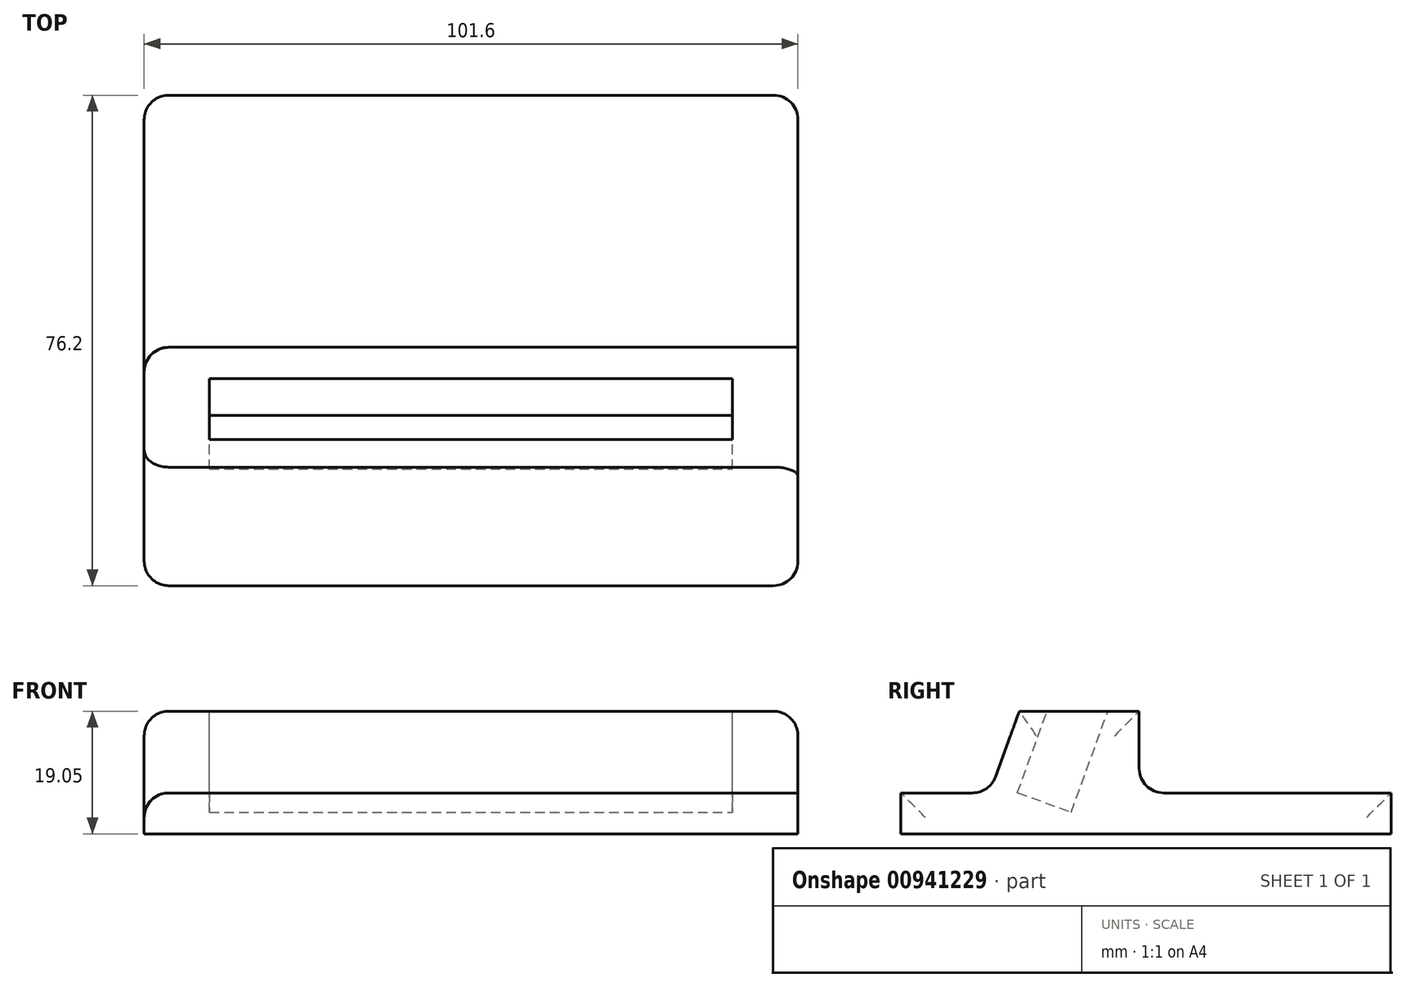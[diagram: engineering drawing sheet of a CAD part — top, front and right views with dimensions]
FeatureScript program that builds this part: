
annotation { "Feature Type Name" : "Feature", "Feature Type Description" : "" }
export const myFeature = defineFeature(function(context is Context, id is Id, definition is map)
    precondition{}
    {
        {
            var Q0;
            Q0=qCreatedBy(makeId("Top.planeOp"),FACE);
            var sketch = newSketch(context, id + "F0", { "sketchPlane" : qUnion([Q0])});
            skLineSegment(sketch, "E0.bottom", {"start": v(-54.82, -43.76) * mm, "end": v(46.78, -43.76) * mm});
            skLineSegment(sketch, "E0.top", {"start": v(-54.82, 32.44) * mm, "end": v(46.78, 32.44) * mm});
            skLineSegment(sketch, "E0.left", {"start": v(-54.82, -43.76) * mm, "end": v(-54.82, 32.44) * mm});
            skLineSegment(sketch, "E0.right", {"start": v(46.78, -43.76) * mm, "end": v(46.78, 32.44) * mm});
            skSolve(sketch);
        }
        {
            var Q0;
            Q0=makeQuery(id+"F0.imprint","IMPRINT",FACE,{"disambiguationData":[TD([[makeQuery(id+"F0.imprint","IMPRINT",EDGE,{"derivedFrom":sQuery(id+"F0.wireOp",EDGE,"E0.bottom")}),1.0]])]});
            extrude(context, id + "F1", {"entities" : qUnion([Q0]), "depth" : 19.05 * mm, "offsetDistance" : 25.4 * mm});
        }
        {
            var Q0;
            Q0=makeQuery(id+"F1.opExtrude","CAP_EDGE",EDGE,{"disambiguationData":[OSD([sQuery(id+"F0.wireOp",EDGE,"E0.top")])],"isStart":false});
            cPlane(context, id + "F2", {"entities" : qUnion([Q0]), "cplaneType" : CPlaneType.LINE_ANGLE, "offset" : 25.4 * mm, "angle" : 70 * degree, "width" : 152.4 * mm, "height" : 152.4 * mm});
        }
        {
            var Q0;
            Q0=qCreatedBy(id+"F2.planeOp",FACE);
            var sketch = newSketch(context, id + "F3", { "sketchPlane" : qUnion([Q0])});
            skLineSegment(sketch, "E1.bottom", {"start": v(-44.66, -26.29) * mm, "end": v(36.62, -26.29) * mm});
            skLineSegment(sketch, "E1.top", {"start": v(-44.66, -17.4) * mm, "end": v(36.62, -17.4) * mm});
            skLineSegment(sketch, "E1.left", {"start": v(-44.66, -26.29) * mm, "end": v(-44.66, -17.4) * mm});
            skLineSegment(sketch, "E1.right", {"start": v(36.62, -26.29) * mm, "end": v(36.62, -17.4) * mm});
            skLineSegment(sketch, "E2", {"start": v(-44.66, -17.4) * mm, "end": v(-54.82, -17.4) * mm, "construction": true});
            skLineSegment(sketch, "E3", {"start": v(36.62, -17.4) * mm, "end": v(46.78, -17.4) * mm, "construction": true});
            skSolve(sketch);
        }
        {
            var Q0;
            Q0=makeQuery(id+"F3.imprint","IMPRINT",FACE,{"disambiguationData":[TD([[makeQuery(id+"F3.imprint","IMPRINT",EDGE,{"derivedFrom":sQuery(id+"F3.wireOp",EDGE,"E1.bottom")}),1.0]])]});
            extrude(context, id + "F4", {"entities" : qUnion([Q0]), "operationType" : NewBodyOperationType.REMOVE, "oppositeDirection" : true, "depth" : 31.75 * mm, "offsetDistance" : 25.4 * mm});
        }
        {
            var Q0;
            Q0=makeQuery(id+"F1.opExtrude","SWEPT_FACE",FACE,{"disambiguationData":[OSD([sQuery(id+"F0.wireOp",EDGE,"E0.right")])]});
            var sketch = newSketch(context, id + "F5", { "sketchPlane" : qUnion([Q0])});
            skLineSegment(sketch, "E4", {"start": v(-6.73, 19.05) * mm, "end": v(-6.73, 6.35) * mm});
            skLineSegment(sketch, "E5", {"start": v(-6.73, 6.35) * mm, "end": v(32.44, 6.35) * mm});
            skLineSegment(sketch, "E6", {"start": v(32.44, 6.35) * mm, "end": v(32.44, 19.05) * mm});
            skLineSegment(sketch, "E7", {"start": v(32.44, 19.05) * mm, "end": v(-6.73, 19.05) * mm});
            skLineSegment(sketch, "E8", {"start": v(-25.35, 19.05) * mm, "end": v(-29.97, 6.35) * mm});
            skLineSegment(sketch, "E9", {"start": v(-29.97, 6.35) * mm, "end": v(-43.76, 6.35) * mm});
            skLineSegment(sketch, "E10", {"start": v(-43.76, 6.35) * mm, "end": v(-43.76, 19.05) * mm});
            skLineSegment(sketch, "E11", {"start": v(-43.76, 19.05) * mm, "end": v(-25.35, 19.05) * mm});
            skSolve(sketch);
        }
        {
            var Q0;
            Q0=makeQuery(id+"F5.imprint","IMPRINT",FACE,{"disambiguationData":[TD([[makeQuery(id+"F5.imprint","IMPRINT",EDGE,{"derivedFrom":sQuery(id+"F5.wireOp",EDGE,"E8")}),-1.0]])]});
            var Q1;
            Q1=makeQuery(id+"F5.imprint","IMPRINT",FACE,{"disambiguationData":[TD([[makeQuery(id+"F5.imprint","IMPRINT",EDGE,{"derivedFrom":sQuery(id+"F5.wireOp",EDGE,"E4")}),1.0]])]});
            extrude(context, id + "F6", {"entities" : qUnion([Q0, Q1]), "operationType" : NewBodyOperationType.REMOVE, "endBound" : BoundingType.THROUGH_ALL, "oppositeDirection" : true, "depth" : 25.4 * mm, "offsetDistance" : 25.4 * mm});
        }
        {
            var Q0;
            Q0=makeQuery(id+"F6.boolean.opBoolean","COPY",EDGE,{"derivedFrom":makeQuery(id+"F6.opExtrude","SWEPT_EDGE",EDGE,{"disambiguationData":[OSD([sQuery(id+"F5.wireOp",EDGE,"E8"),sQuery(id+"F5.wireOp",EDGE,"E9")])]})});
            var Q1;
            Q1=makeQuery(id+"F6.boolean.opBoolean","COPY",EDGE,{"derivedFrom":makeQuery(id+"F6.opExtrude","SWEPT_EDGE",EDGE,{"disambiguationData":[OSD([sQuery(id+"F0.wireOp",EDGE,"E0.right"),sQuery(id+"F5.wireOp",EDGE,"E8"),sQuery(id+"F5.wireOp",EDGE,"E11")])]})});
            var Q2;
            Q2=makeQuery(id+"F6.boolean.opBoolean","COPY",EDGE,{"derivedFrom":makeQuery(id+"F6.opExtrude","SWEPT_EDGE",EDGE,{"disambiguationData":[OSD([sQuery(id+"F0.wireOp",EDGE,"E0.right"),sQuery(id+"F5.wireOp",EDGE,"E4"),sQuery(id+"F5.wireOp",EDGE,"E7")])]})});
            var Q3;
            Q3=makeQuery(id+"F6.boolean.opBoolean","COPY",EDGE,{"derivedFrom":makeQuery(id+"F6.opExtrude","SWEPT_EDGE",EDGE,{"disambiguationData":[OSD([sQuery(id+"F5.wireOp",EDGE,"E4"),sQuery(id+"F5.wireOp",EDGE,"E5")])]})});
            var Q4;
            Q4=makeQuery(id+"F6.boolean.opBoolean","COPY",EDGE,{"derivedFrom":makeQuery(id+"F6.opExtrude","CAP_EDGE",EDGE,{"disambiguationData":[OSD([sQuery(id+"F5.wireOp",EDGE,"E9")])],"isStart":true})});
            var Q5;
            Q5=makeQuery(id+"F6.boolean.opBoolean","COPY",EDGE,{"derivedFrom":makeQuery(id+"F6.opExtrude","SWEPT_EDGE",EDGE,{"disambiguationData":[OSD([sQuery(id+"F0.wireOp",EDGE,"E0.bottom"),sQuery(id+"F0.wireOp",EDGE,"E0.right"),sQuery(id+"F5.wireOp",EDGE,"E9"),sQuery(id+"F5.wireOp",EDGE,"E10")])]})});
            var Q6;
            Q6=makeQuery(id+"F6.boolean.opBoolean","INTERSECT",EDGE,{"derivedFrom":[makeQuery(id+"F1.opExtrude","SWEPT_FACE",FACE,{"disambiguationData":[OSD([sQuery(id+"F0.wireOp",EDGE,"E0.left")])]}),makeQuery(id+"F6.opExtrude","SWEPT_FACE",FACE,{"disambiguationData":[OSD([sQuery(id+"F5.wireOp",EDGE,"E9")])]})]});
            var Q7;
            Q7=makeQuery(id+"F6.boolean.opBoolean","INTERSECT",EDGE,{"derivedFrom":[makeQuery(id+"F1.opExtrude","SWEPT_FACE",FACE,{"disambiguationData":[OSD([sQuery(id+"F0.wireOp",EDGE,"E0.left")])]}),makeQuery(id+"F6.opExtrude","SWEPT_FACE",FACE,{"disambiguationData":[OSD([sQuery(id+"F5.wireOp",EDGE,"E5")])]})]});
            var Q8;
            Q8=makeQuery(id+"F6.boolean.opBoolean","COPY",EDGE,{"derivedFrom":makeQuery(id+"F6.opExtrude","SWEPT_EDGE",EDGE,{"disambiguationData":[OSD([sQuery(id+"F0.wireOp",EDGE,"E0.top"),sQuery(id+"F0.wireOp",EDGE,"E0.right"),sQuery(id+"F5.wireOp",EDGE,"E5"),sQuery(id+"F5.wireOp",EDGE,"E6")])]})});
            var Q9;
            Q9=makeQuery(id+"F6.boolean.opBoolean","COPY",EDGE,{"derivedFrom":makeQuery(id+"F6.opExtrude","CAP_EDGE",EDGE,{"disambiguationData":[OSD([sQuery(id+"F5.wireOp",EDGE,"E5")])],"isStart":true})});
            var Q10;
            Q10=makeQuery(id+"F1.opExtrude","SWEPT_EDGE",EDGE,{"disambiguationData":[OSD([sQuery(id+"F0.wireOp",EDGE,"E0.top"),sQuery(id+"F0.wireOp",EDGE,"E0.right")])]});
            var Q11;
            Q11=makeQuery(id+"F1.opExtrude","SWEPT_EDGE",EDGE,{"disambiguationData":[OSD([sQuery(id+"F0.wireOp",EDGE,"E0.bottom"),sQuery(id+"F0.wireOp",EDGE,"E0.right")])]});
            var Q12;
            Q12=makeQuery(id+"F1.opExtrude","SWEPT_EDGE",EDGE,{"disambiguationData":[OSD([sQuery(id+"F0.wireOp",EDGE,"E0.bottom"),sQuery(id+"F0.wireOp",EDGE,"E0.left")])]});
            var Q13;
            Q13=makeQuery(id+"F6.boolean.opBoolean","INTERSECT",EDGE,{"derivedFrom":[makeQuery(id+"F1.opExtrude","SWEPT_FACE",FACE,{"disambiguationData":[OSD([sQuery(id+"F0.wireOp",EDGE,"E0.left")])]}),makeQuery(id+"F6.opExtrude","SWEPT_FACE",FACE,{"disambiguationData":[OSD([sQuery(id+"F5.wireOp",EDGE,"E8")])]})]});
            var Q14;
            Q14=makeQuery(id+"F6.boolean.opBoolean","INTERSECT",EDGE,{"derivedFrom":[makeQuery(id+"F1.opExtrude","SWEPT_FACE",FACE,{"disambiguationData":[OSD([sQuery(id+"F0.wireOp",EDGE,"E0.left")])]}),makeQuery(id+"F6.opExtrude","SWEPT_FACE",FACE,{"disambiguationData":[OSD([sQuery(id+"F5.wireOp",EDGE,"E4")])]})]});
            var Q15;
            Q15=makeQuery(id+"F6.boolean.opBoolean","COPY",EDGE,{"derivedFrom":makeQuery(id+"F6.opExtrude","CAP_EDGE",EDGE,{"disambiguationData":[OSD([sQuery(id+"F5.wireOp",EDGE,"E8")])],"isStart":true})});
            var Q16;
            Q16=makeQuery(id+"F1.opExtrude","CAP_EDGE",EDGE,{"disambiguationData":[OSD([sQuery(id+"F0.wireOp",EDGE,"E0.right")])],"isStart":false});
            var Q17;
            Q17=makeQuery(id+"F1.opExtrude","CAP_EDGE",EDGE,{"disambiguationData":[OSD([sQuery(id+"F0.wireOp",EDGE,"E0.left")])],"isStart":false});
            var Q18;
            Q18=makeQuery(id+"F1.opExtrude","SWEPT_EDGE",EDGE,{"disambiguationData":[OSD([sQuery(id+"F0.wireOp",EDGE,"E0.top"),sQuery(id+"F0.wireOp",EDGE,"E0.left")])]});
            fillet(context, id + "F7", {"entities" : qUnion([Q0, Q1, Q2, Q3, Q4, Q5, Q6, Q7, Q8, Q9, Q10, Q11, Q12, Q13, Q14, Q15, Q16, Q17, Q18]), "radius" : 3.8 * mm, "tangentPropagation" : true, "allowEdgeOverflow" : false});
        }
    });
